# Revit family: Haworth_Mex-Hi_OccasionalTable
name_source: partatom
category: Furniture
revit_build: Autodesk Revit 2018 (Build: 20170223_1515(x64)
units: mm (PartAtom-declared; Revit-internal decimal feet)

## family parameters
Always vertical = Yes
Cut with Voids When Loaded = No
OmniClass Number = 23.40.70.14.64.21
OmniClass Title = Systems Furniture
Room Calculation Point = No
Shared = No
Work Plane-Based = No

## types (4) — shared parameters
Assembly Code = E2020200
Description = Haworth - Cassina - Mex-Hi - Occasional Table
Manufacturer = Haworth
Model = HCCSMHTO
Revision Number = 1
Size = Verify Final Dim. w/ Haworth
Sustainability Info = https://www.haworth.com
Tray Width = 15.7 "
URL = https://www.haworth.com
URL - Product = https://www.haworth.com
Warranty = http://www.haworth.com

## per-type parameters (varying)
| type | Actual Depth | Actual Height | Actual Width | Large | Large w/Wood Tray | Small | Stone Top | Top Offset | Tray Depth | Wood Tray |
| Small with Wood Tray | 15.7 " | 14.2 " | 35.4 " | No | No | Yes | No | 12.69 " | 15.7 " | Yes |
| Small with Stone Top | 15.7 " | 14.2 " | 35.4 " | No | No | Yes | Yes | 12.69 " | 15.7 " | No |
| Large with Stone Top and Wood Tray | 43.3 " | 8.7 " | 51.2 " | Yes | Yes | No | Yes | 8.89 " | 43.3 " | No |
| Large with Stone Top | 43.3 " | 8.7 " | 51.2 " | Yes | No | No | Yes | 8.89 " | 43.3 " | No |

## geometry (parser evidence)
native form markers: Sweep x11
no freeform markers — native parametric forms only
